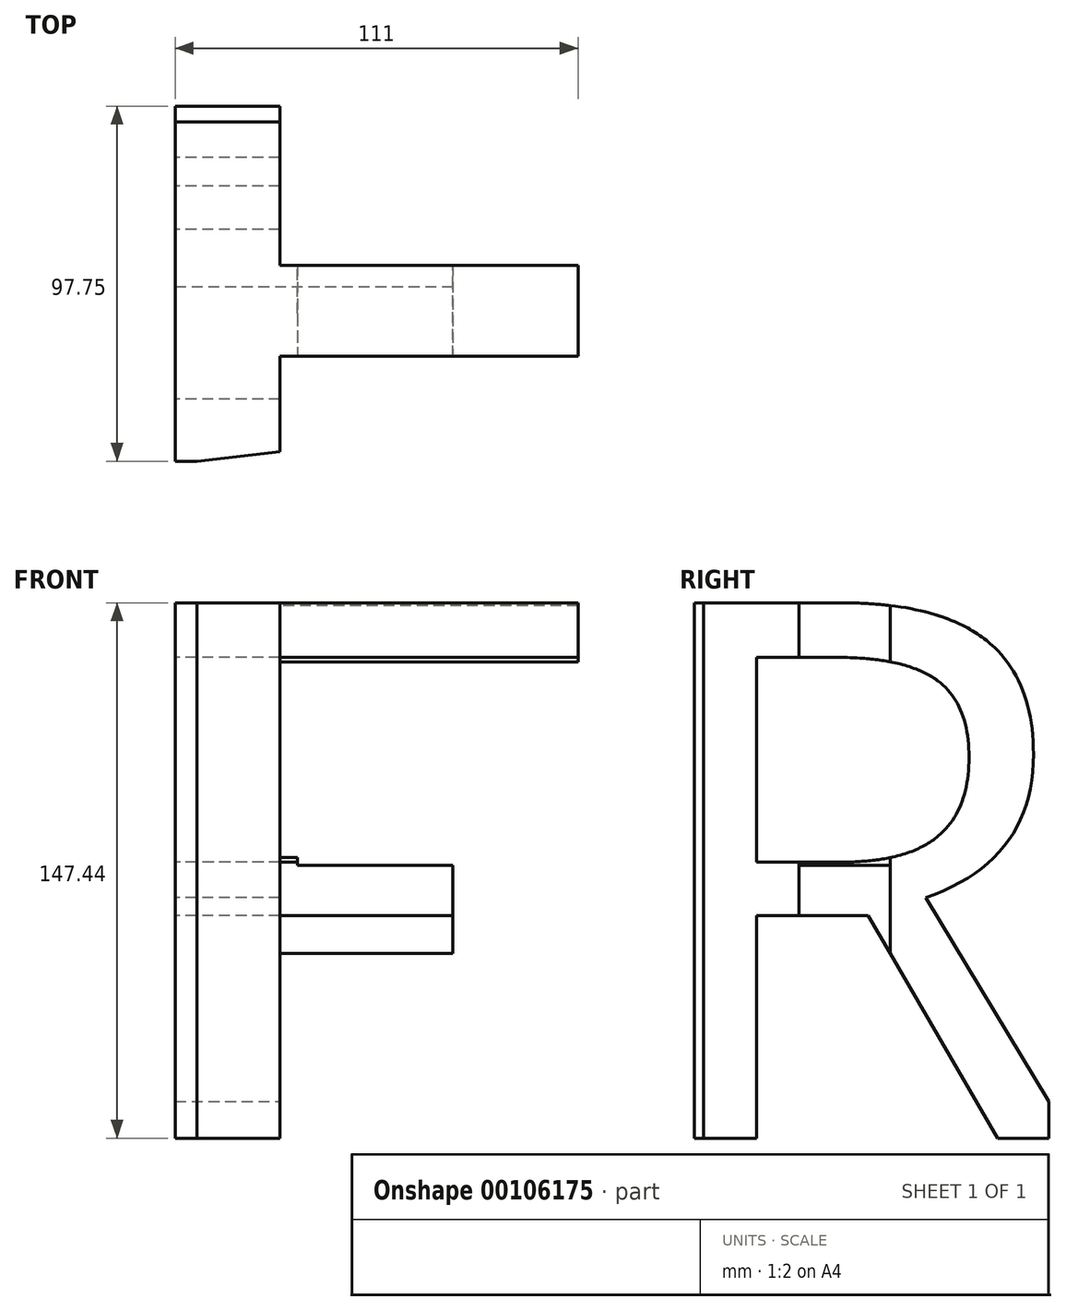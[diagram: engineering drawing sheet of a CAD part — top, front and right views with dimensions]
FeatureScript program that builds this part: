
annotation { "Feature Type Name" : "Feature", "Feature Type Description" : "" }
export const myFeature = defineFeature(function(context is Context, id is Id, definition is map)
    precondition{}
    {
        {
            var Q0;
            Q0=qCreatedBy(makeId("Right.planeOp"),FACE);
            var sketch = newSketch(context, id + "F0", { "sketchPlane" : qUnion([Q0])});
            skText(sketch, "E0", { "text": "R", "fontName": "OpenSans-Regular.ttf"});
            const initialGuessF0  = {"E0": [-0.07424, -0.07511, 1, 0, 0.1487]};
            skSetInitialGuess(sketch, initialGuessF0);
            skSolve(sketch);
        }
        {
            var Q0;
            Q0 = qSketchRegion(id + "F0", true);
            extrude(context, id + "F1", {"entities" : qUnion([Q0]), "depth" : 111 * mm});
        }
        {
            var Q0;
            Q0=makeQuery(id+"F1.opExtrude","SWEPT_FACE",FACE,{"disambiguationData":[OSD([sQuery(id+"F0.wireOp",EDGE,"E0.sketch_text.stroke-2")])]});
            var sketch = newSketch(context, id + "F2", { "sketchPlane" : qUnion([Q0])});
            skLineSegment(sketch, "E1", {"start": v(0, -75.11) * mm, "end": v(0, 72.32) * mm});
            skLineSegment(sketch, "E2", {"start": v(0, 72.32) * mm, "end": v(111, 72.32) * mm});
            skLineSegment(sketch, "E3", {"start": v(111, 72.32) * mm, "end": v(111, 37.68) * mm});
            skLineSegment(sketch, "E4", {"start": v(111, 37.68) * mm, "end": v(33.7, 37.68) * mm});
            skLineSegment(sketch, "E5", {"start": v(33.7, 37.68) * mm, "end": v(33.7, 0) * mm});
            skLineSegment(sketch, "E6", {"start": v(33.7, 0) * mm, "end": v(76.56, 0) * mm});
            skLineSegment(sketch, "E7", {"start": v(76.56, 0) * mm, "end": v(76.56, -30.34) * mm});
            skLineSegment(sketch, "E8", {"start": v(76.56, -30.34) * mm, "end": v(33.7, -30.34) * mm});
            skLineSegment(sketch, "E9", {"start": v(33.7, -30.34) * mm, "end": v(33.7, -75.11) * mm});
            skLineSegment(sketch, "E10", {"start": v(33.7, -75.11) * mm, "end": v(0, -75.11) * mm});
            skSolve(sketch);
        }
        {
            var Q0;
            Q0 = qSketchRegion(id + "F2", true);
            extrude(context, id + "F3", {"entities" : qUnion([Q0]), "operationType" : NewBodyOperationType.INTERSECT, "oppositeDirection" : true, "depth" : 333 * mm});
        }
        {
            var Q0;
            Q0=makeQuery(id+"F1.opExtrude","SWEPT_FACE",FACE,{"disambiguationData":[OSD([sQuery(id+"F0.wireOp",EDGE,"E0.sketch_text.stroke-3")])]});
            var sketch = newSketch(context, id + "F4", { "sketchPlane" : qUnion([Q0])});
            skSolve(sketch);
        }
        {
            var Q0;
            {var subQ0=sQuery(id+"F0.wireOp",EDGE,"E0.sketch_text.stroke-3");Q0=makeQuery(id+"F4.imprint","IMPRINT",FACE,{"disambiguationData":[TD([[makeQuery(id+"F4.imprint","IMPRINT",EDGE,{"derivedFrom":makeQuery(id+"F1.opExtrude","CAP_EDGE",EDGE,{"disambiguationData":[OSD([subQ0])],"isStart":true})}),-1.0]])]});}
            var sketch = newSketch(context, id + "F5", { "sketchPlane" : qUnion([Q0])});
            skLineSegment(sketch, "E11", {"start": v(0, -54.66) * mm, "end": v(0, 43.78) * mm});
            skLineSegment(sketch, "E12", {"start": v(0, 43.78) * mm, "end": v(28.88, 43.78) * mm});
            skLineSegment(sketch, "E13", {"start": v(28.88, 43.78) * mm, "end": v(28.88, 0) * mm});
            skLineSegment(sketch, "E14", {"start": v(28.88, 0) * mm, "end": v(113.67, 0) * mm});
            skLineSegment(sketch, "E15", {"start": v(113.67, 0) * mm, "end": v(113.67, -25.12) * mm});
            skLineSegment(sketch, "E16", {"start": v(113.67, -25.12) * mm, "end": v(28.88, -25.12) * mm});
            skLineSegment(sketch, "E17", {"start": v(28.88, -25.12) * mm, "end": v(28.88, -51.36) * mm});
            skLineSegment(sketch, "E18", {"start": v(28.88, -51.36) * mm, "end": v(0, -54.66) * mm});
            skSolve(sketch);
        }
        {
            var Q0;
            Q0 = qSketchRegion(id + "F5", true);
            extrude(context, id + "F6", {"entities" : qUnion([Q0]), "operationType" : NewBodyOperationType.INTERSECT, "oppositeDirection" : true, "depth" : 292.2 * mm});
        }
    });
